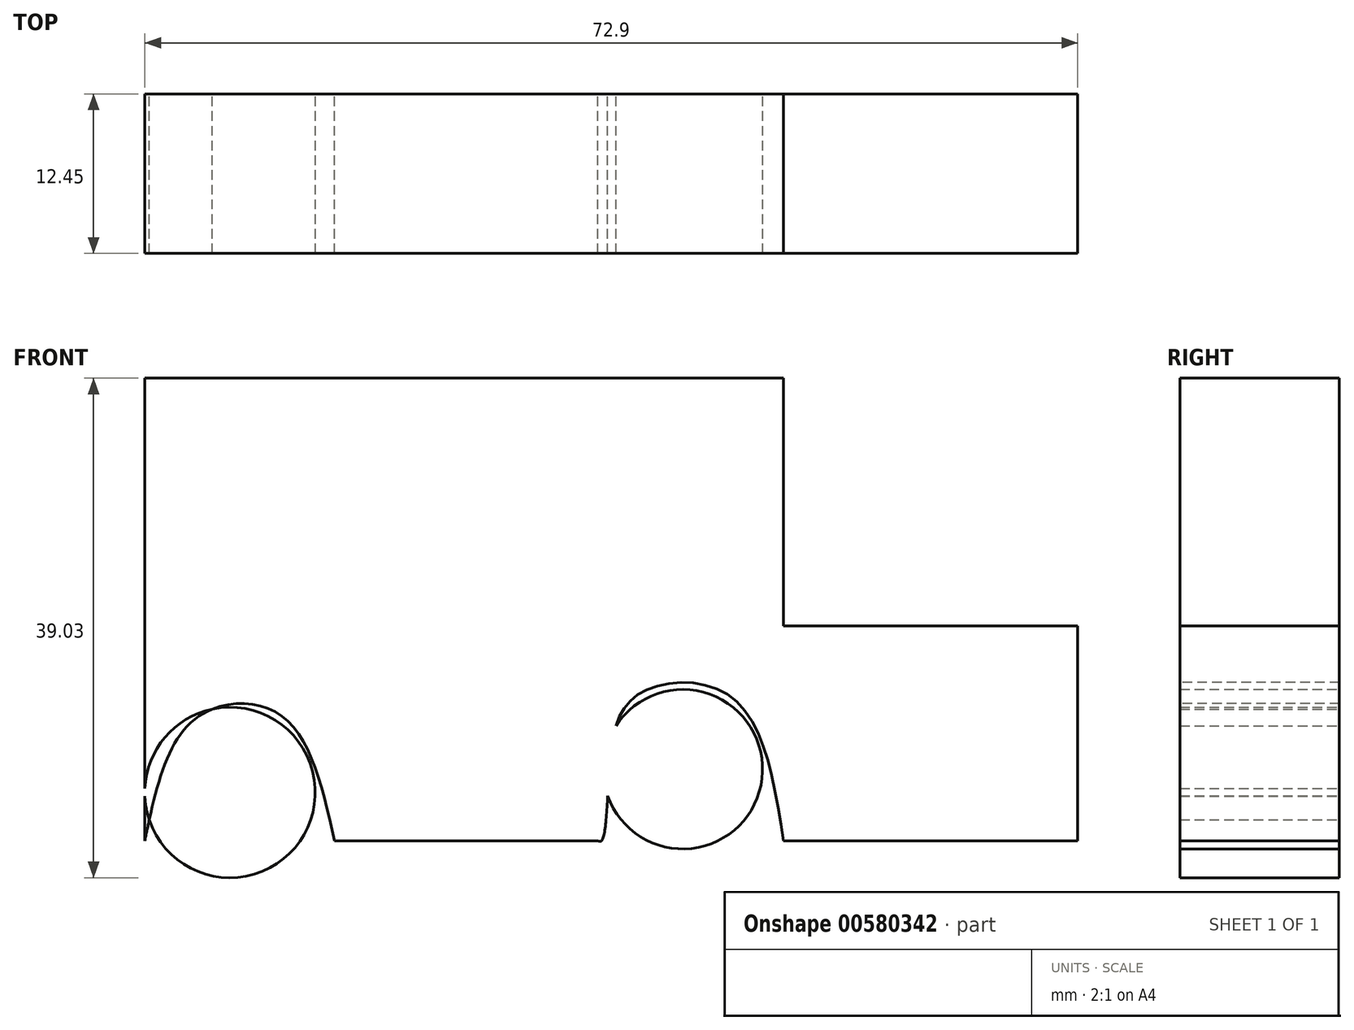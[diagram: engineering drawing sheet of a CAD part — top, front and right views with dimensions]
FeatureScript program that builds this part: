
annotation { "Feature Type Name" : "Feature", "Feature Type Description" : "" }
export const myFeature = defineFeature(function(context is Context, id is Id, definition is map)
    precondition{}
    {
        {
            var Q0;
            Q0=qCreatedBy(makeId("Front.planeOp"),FACE);
            var sketch = newSketch(context, id + "F0", { "sketchPlane" : qUnion([Q0])});
            skLineSegment(sketch, "E0", {"start": v(-49.91, 0) * mm, "end": v(-49.91, 36.15) * mm});
            skLineSegment(sketch, "E1", {"start": v(-49.91, 36.15) * mm, "end": v(-13.61, 36.15) * mm});
            skLineSegment(sketch, "E2", {"start": v(-13.61, 36.15) * mm, "end": v(0, 36.15) * mm});
            skLineSegment(sketch, "E3", {"start": v(0, 36.15) * mm, "end": v(0, 16.79) * mm});
            skLineSegment(sketch, "E4", {"start": v(0, 16.79) * mm, "end": v(22.99, 16.79) * mm});
            skLineSegment(sketch, "E5", {"start": v(22.99, 16.79) * mm, "end": v(22.99, 0) * mm});
            skLineSegment(sketch, "E6", {"start": v(22.99, 0) * mm, "end": v(0, 0) * mm});
            skFitSpline(sketch, "E7", {"points": [v(0, 0) * mm, v(-4.23, 11.34) * mm, v(-11.5, 11.34) * mm, v(-13.61, 5.6) * mm, v(-14.22, 0) * mm, v(-14.52, 0) * mm], "startDerivative": vector(-7.37, 47.06) * mm, "endDerivative": vector(-6.74, 2.75) * mm});
            skLineSegment(sketch, "E8", {"start": v(-14.22, 0) * mm, "end": v(-35.09, 0) * mm});
            skFitSpline(sketch, "E9", {"points": [v(-35.09, 0) * mm, v(-39.32, 9.83) * mm, v(-45.98, 9.53) * mm, v(-49.91, 0) * mm], "startDerivative": vector(-7.5, 33.86) * mm, "endDerivative": vector(-6.78, -32.61) * mm});
            skPoint(sketch, "E10.1.internal.snap0", {"position": v(11.5, 16.79) * mm});
            skFitSpline(sketch, "E10", {"points": [v(11.5, 16.79) * mm, v(11.5, 26.77) * mm, v(16.64, 31.3) * mm, v(21.48, 31.61) * mm, v(20.87, 31.61) * mm, v(21.17, 31.61) * mm], "startDerivative": vector(-4.12, 32.05) * mm, "endDerivative": vector(8.64, -0.05) * mm});
            skFitSpline(sketch, "E11", {"points": [v(16.03, 16.79) * mm, v(16.33, 25.86) * mm, v(19.96, 27.68) * mm, v(22.99, 27.38) * mm], "startDerivative": vector(-3, 24.3) * mm, "endDerivative": vector(11.07, -2.26) * mm});
            skFitSpline(sketch, "E12", {"points": [v(22.04, 27.57) * mm, v(21.48, 31.61) * mm], "startDerivative": vector(-0.56, 4.04) * mm, "endDerivative": vector(-0.56, 4.04) * mm});
            skCircle(sketch, "E13", {"center": v(-43.26, 3.78) * mm, "radius": 6.66 * mm});
            skCircle(sketch, "E14", {"center": v(-7.86, 5.6) * mm, "radius": 6.23 * mm});
            skLineSegment(sketch, "E15.top", {"start": v(-13.61, 16.79) * mm, "end": v(0, 16.79) * mm});
            skLineSegment(sketch, "E15.left", {"start": v(-13.61, 36.15) * mm, "end": v(-13.61, 16.79) * mm});
            skLineSegment(sketch, "E16.bottom", {"start": v(-13.61, 36.15) * mm, "end": v(-19.66, 36.15) * mm});
            skLineSegment(sketch, "E16.top", {"start": v(-13.61, 41.9) * mm, "end": v(-19.66, 41.9) * mm});
            skLineSegment(sketch, "E16.left", {"start": v(-13.61, 36.15) * mm, "end": v(-13.61, 41.9) * mm});
            skLineSegment(sketch, "E16.right", {"start": v(-19.66, 36.15) * mm, "end": v(-19.66, 41.9) * mm});
            skSolve(sketch);
        }
        {
            var Q0;
            {var subQ0=sQuery(id+"F0.wireOp",EDGE,"E9");var subQ1=sQuery(id+"F0.wireOp",EDGE,"E0");var subQ2=makeQuery(id+"F0.imprint","INTERSECT",VERTEX,{"derivedFrom":[subQ1,subQ0]});Q0=makeQuery(id+"F0.imprint","IMPRINT",FACE,{"disambiguationData":[TD([[makeQuery(id+"F0.imprint","IMPRINT",EDGE,{"disambiguationData":[TD([[subQ2,-1.0]])],"derivedFrom":subQ1}),-1.0]])]});}
            var Q1;
            {var subQ0=sQuery(id+"F0.wireOp",EDGE,"E13");var subQ1=sQuery(id+"F0.wireOp",EDGE,"E0");var subQ2=makeQuery(id+"F0.imprint","INTERSECT",VERTEX,{"disambiguationData":[OD(0.0)],"derivedFrom":[subQ1,subQ0]});Q1=makeQuery(id+"F0.imprint","IMPRINT",FACE,{"disambiguationData":[TD([[makeQuery(id+"F0.imprint","IMPRINT",EDGE,{"disambiguationData":[TD([[subQ2,-1.0]])],"derivedFrom":subQ1}),1.0]])]});}
            var Q2;
            {var subQ0=sQuery(id+"F0.wireOp",EDGE,"E14");var subQ1=sQuery(id+"F0.wireOp",EDGE,"E7");var subQ2=makeQuery(id+"F0.imprint","INTERSECT",VERTEX,{"disambiguationData":[OD(0.0)],"derivedFrom":[subQ1,subQ0]});Q2=makeQuery(id+"F0.imprint","IMPRINT",FACE,{"disambiguationData":[TD([[makeQuery(id+"F0.imprint","IMPRINT",EDGE,{"disambiguationData":[TD([[subQ2,-1.0]])],"derivedFrom":subQ1}),1.0]])]});}
            var Q3;
            {var subQ0=sQuery(id+"F0.wireOp",EDGE,"E8");var subQ1=sQuery(id+"F0.wireOp",EDGE,"E7");var subQ2=makeQuery(id+"F0.imprint","INTERSECT",VERTEX,{"disambiguationData":[OD(0.0)],"derivedFrom":[subQ1,subQ0]});Q3=makeQuery(id+"F0.imprint","IMPRINT",FACE,{"disambiguationData":[TD([[makeQuery(id+"F0.imprint","IMPRINT",EDGE,{"disambiguationData":[TD([[subQ2,1.0]])],"derivedFrom":subQ1}),-1.0]])]});}
            var Q4;
            {var subQ0=sQuery(id+"F0.wireOp",EDGE,"E13");var subQ1=sQuery(id+"F0.wireOp",EDGE,"E9");var subQ2=makeQuery(id+"F0.imprint","INTERSECT",VERTEX,{"disambiguationData":[OD(0.0)],"derivedFrom":[subQ1,subQ0]});Q4=makeQuery(id+"F0.imprint","IMPRINT",FACE,{"disambiguationData":[TD([[makeQuery(id+"F0.imprint","IMPRINT",EDGE,{"disambiguationData":[TD([[subQ2,-1.0]])],"derivedFrom":subQ1}),1.0]])]});}
            var Q5;
            Q5=makeQuery(id+"F0.imprint","IMPRINT",FACE,{"disambiguationData":[TD([[makeQuery(id+"F0.imprint","IMPRINT",EDGE,{"derivedFrom":sQuery(id+"F0.wireOp",EDGE,"E2")}),-1.0]])]});
            var Q6;
            Q6=makeQuery(id+"F0.imprint","IMPRINT",FACE,{"disambiguationData":[TD([[makeQuery(id+"F0.imprint","IMPRINT",EDGE,{"derivedFrom":sQuery(id+"F0.wireOp",EDGE,"E16.bottom")}),-1.0]])]});
            var Q7;
            {var subQ0=sQuery(id+"F0.wireOp",EDGE,"E14");var subQ1=sQuery(id+"F0.wireOp",EDGE,"E7");var subQ2=makeQuery(id+"F0.imprint","INTERSECT",VERTEX,{"disambiguationData":[OD(0.0)],"derivedFrom":[subQ1,subQ0]});Q7=makeQuery(id+"F0.imprint","IMPRINT",FACE,{"disambiguationData":[TD([[makeQuery(id+"F0.imprint","IMPRINT",EDGE,{"disambiguationData":[TD([[subQ2,-1.0]])],"derivedFrom":subQ1}),-1.0]])]});}
            var Q8;
            {var subQ0=sQuery(id+"F0.wireOp",EDGE,"E13");var subQ1=sQuery(id+"F0.wireOp",EDGE,"E0");var subQ2=makeQuery(id+"F0.imprint","INTERSECT",VERTEX,{"disambiguationData":[OD(0.0)],"derivedFrom":[subQ1,subQ0]});Q8=makeQuery(id+"F0.imprint","IMPRINT",FACE,{"disambiguationData":[TD([[makeQuery(id+"F0.imprint","IMPRINT",EDGE,{"disambiguationData":[TD([[subQ2,-1.0]])],"derivedFrom":subQ1}),-1.0]])]});}
            extrude(context, id + "F1", {"entities" : qUnion([Q0, Q1, Q2, Q3, Q4, Q5, Q6, Q7, Q8]), "depth" : 12.45 * mm, "offsetDistance" : 25.4 * mm});
        }
    });
